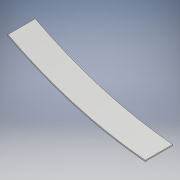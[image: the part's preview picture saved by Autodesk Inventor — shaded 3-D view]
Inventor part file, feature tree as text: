
AUTODESK INVENTOR PART (.ipt)
format: ipt  version: 2018 (Build 220112000, 112)  size: 130,048 bytes
history: native  units: mm
features: other x4, projected_geometry x2, extrude x1, sketch x1
ambient origin geometry x8: Origin, YZ Plane, XZ Plane, XY Plane, X Axis, Y Axis, Z Axis, Center Point
bodies: Body1 (feature_tree)
feature tree (8):
  other  "splitter.ipt"
  extrude  "押し出し2"  Depth=10.0mm
  other  "ソリッド162::splitter.ipt"
  other  "TaggingFeature1"
  sketch  "スケッチ2"
  projected_geometry  "投影ループ2"
  projected_geometry  "投影ループ3"
  other  "ソリッド1"
